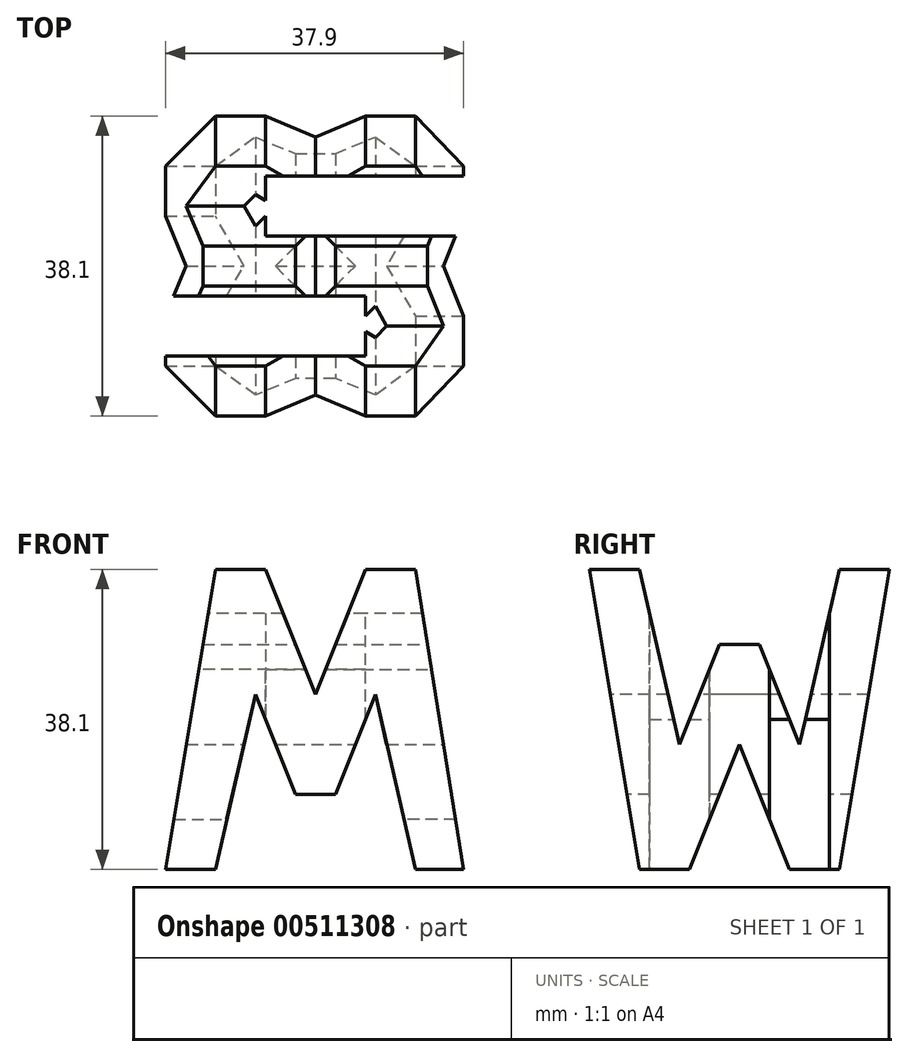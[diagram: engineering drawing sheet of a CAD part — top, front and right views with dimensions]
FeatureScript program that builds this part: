
annotation { "Feature Type Name" : "Feature", "Feature Type Description" : "" }
export const myFeature = defineFeature(function(context is Context, id is Id, definition is map)
    precondition{}
    {
        {
            var Q0;
            Q0=qCreatedBy(makeId("Front.planeOp"),FACE);
            var sketch = newSketch(context, id + "F0", { "sketchPlane" : qUnion([Q0])});
            skLineSegment(sketch, "E0", {"start": v(0, 0) * mm, "end": v(0, 38.1) * mm});
            skLineSegment(sketch, "E1", {"start": v(0, 38.1) * mm, "end": v(38.1, 38.1) * mm});
            skLineSegment(sketch, "E2", {"start": v(38.1, 38.1) * mm, "end": v(38.1, 0) * mm});
            skLineSegment(sketch, "E3", {"start": v(38.1, 0) * mm, "end": v(0, 0) * mm});
            skSolve(sketch);
        }
        {
            var Q0;
            Q0 = qSketchRegion(id + "F0", true);
            extrude(context, id + "F1", {"entities" : qUnion([Q0]), "depth" : 38.1 * mm, "offsetDistance" : 25.4 * mm});
        }
        {
            var Q0;
            Q0=qCreatedBy(makeId("Front.planeOp"),FACE);
            cPlane(context, id + "F2", {"entities" : qUnion([Q0]), "cplaneType" : CPlaneType.OFFSET, "offset" : 38.1 * mm, "width" : 152.4 * mm, "height" : 152.4 * mm});
        }
        {
            var Q0;
            Q0=qCreatedBy(makeId("Top.planeOp"),FACE);
            cPlane(context, id + "F3", {"entities" : qUnion([Q0]), "cplaneType" : CPlaneType.OFFSET, "offset" : 38.1 * mm, "width" : 152.4 * mm, "height" : 152.4 * mm});
        }
        {
            var Q0;
            Q0=makeQuery(id+"F1.opExtrude","SWEPT_FACE",FACE,{"disambiguationData":[OSD([sQuery(id+"F0.wireOp",EDGE,"E2")])]});
            var sketch = newSketch(context, id + "F4", { "sketchPlane" : qUnion([Q0])});
            skLineSegment(sketch, "E4", {"start": v(-38.1, 38.1) * mm, "end": v(-31.75, 38.1) * mm});
            skLineSegment(sketch, "E5", {"start": v(-31.75, 38.1) * mm, "end": v(-26.67, 15.88) * mm});
            skLineSegment(sketch, "E6", {"start": v(-38.1, 38.1) * mm, "end": v(-31.75, 0) * mm});
            skLineSegment(sketch, "E7", {"start": v(-31.75, 0) * mm, "end": v(-25.4, 0) * mm});
            skLineSegment(sketch, "E8", {"start": v(-25.4, 0) * mm, "end": v(-19.05, 15.88) * mm});
            skLineSegment(sketch, "E9", {"start": v(-19.05, 15.88) * mm, "end": v(-12.7, 0) * mm});
            skLineSegment(sketch, "E10", {"start": v(-12.7, 0) * mm, "end": v(-6.35, 0) * mm});
            skLineSegment(sketch, "E11", {"start": v(-6.35, 0) * mm, "end": v(0, 38.1) * mm});
            skLineSegment(sketch, "E12", {"start": v(0, 38.1) * mm, "end": v(-6.35, 38.1) * mm});
            skLineSegment(sketch, "E13", {"start": v(-6.35, 38.1) * mm, "end": v(-11.43, 15.88) * mm});
            skLineSegment(sketch, "E14", {"start": v(-11.43, 15.88) * mm, "end": v(-16.5, 28.58) * mm});
            skLineSegment(sketch, "E15", {"start": v(-16.5, 28.58) * mm, "end": v(-21.59, 28.58) * mm});
            skLineSegment(sketch, "E16", {"start": v(-21.59, 28.58) * mm, "end": v(-26.67, 15.88) * mm});
            skSolve(sketch);
        }
        {
            var Q0;
            {var subQ1=sQuery(id+"F4.wireOp",EDGE,"E5");Q0=makeQuery(id+"F4.imprint","IMPRINT",FACE,{"disambiguationData":[TD([[makeQuery(id+"F4.imprint","IMPRINT",EDGE,{"derivedFrom":subQ1}),1.0]])]});}
            var Q1;
            {var subQ0=sQuery(id+"F4.wireOp",EDGE,"E6");Q1=makeQuery(id+"F4.imprint","IMPRINT",FACE,{"disambiguationData":[TD([[makeQuery(id+"F4.imprint","IMPRINT",EDGE,{"derivedFrom":subQ0}),-1.0]])]});}
            var Q2;
            {var subQ0=sQuery(id+"F4.wireOp",EDGE,"E8");Q2=makeQuery(id+"F4.imprint","IMPRINT",FACE,{"disambiguationData":[TD([[makeQuery(id+"F4.imprint","IMPRINT",EDGE,{"derivedFrom":subQ0}),-1.0]])]});}
            var Q3;
            {var subQ0=sQuery(id+"F4.wireOp",EDGE,"E11");Q3=makeQuery(id+"F4.imprint","IMPRINT",FACE,{"disambiguationData":[TD([[makeQuery(id+"F4.imprint","IMPRINT",EDGE,{"derivedFrom":subQ0}),-1.0]])]});}
            extrude(context, id + "F5", {"entities" : qUnion([Q0, Q1, Q2, Q3]), "operationType" : NewBodyOperationType.REMOVE, "oppositeDirection" : true, "depth" : 38.1 * mm, "offsetDistance" : 25.4 * mm});
        }
        {
            var Q0;
            Q0=qCreatedBy(id+"F2.planeOp",FACE);
            var sketch = newSketch(context, id + "F6", { "sketchPlane" : qUnion([Q0])});
            skLineSegment(sketch, "E17", {"start": v(6.35, 38.1) * mm, "end": v(12.7, 38.1) * mm});
            skLineSegment(sketch, "E18", {"start": v(12.7, 38.1) * mm, "end": v(19.05, 22.22) * mm});
            skLineSegment(sketch, "E19", {"start": v(19.05, 22.22) * mm, "end": v(25.4, 38.1) * mm});
            skLineSegment(sketch, "E20", {"start": v(25.4, 38.1) * mm, "end": v(31.75, 38.1) * mm});
            skLineSegment(sketch, "E21", {"start": v(31.75, 38.1) * mm, "end": v(37.9, 0) * mm});
            skLineSegment(sketch, "E22", {"start": v(37.9, 0) * mm, "end": v(31.75, 0) * mm});
            skLineSegment(sketch, "E23", {"start": v(31.75, 0) * mm, "end": v(26.67, 22.22) * mm});
            skLineSegment(sketch, "E24", {"start": v(26.67, 22.22) * mm, "end": v(21.6, 9.52) * mm});
            skLineSegment(sketch, "E25", {"start": v(21.59, 9.52) * mm, "end": v(16.51, 9.52) * mm});
            skLineSegment(sketch, "E26", {"start": v(16.51, 9.52) * mm, "end": v(11.43, 22.22) * mm});
            skLineSegment(sketch, "E27", {"start": v(11.43, 22.22) * mm, "end": v(6.35, 0) * mm});
            skLineSegment(sketch, "E28", {"start": v(6.35, 0) * mm, "end": v(0, 0) * mm});
            skLineSegment(sketch, "E29", {"start": v(0, 0) * mm, "end": v(6.35, 38.1) * mm});
            skLineSegment(sketch, "E30.bottom", {"start": v(0, 0) * mm, "end": v(38.1, 0) * mm});
            skLineSegment(sketch, "E30.top", {"start": v(0, 38.1) * mm, "end": v(38.1, 38.1) * mm});
            skLineSegment(sketch, "E30.left", {"start": v(0, 0) * mm, "end": v(0, 38.1) * mm});
            skLineSegment(sketch, "E30.right", {"start": v(38.1, 0) * mm, "end": v(38.1, 38.1) * mm});
            skSolve(sketch);
        }
        {
            var Q0;
            {var subQ0=sQuery(id+"F6.wireOp",EDGE,"E29");Q0=makeQuery(id+"F6.imprint","IMPRINT",FACE,{"disambiguationData":[TD([[makeQuery(id+"F6.imprint","IMPRINT",EDGE,{"derivedFrom":subQ0}),1.0]])]});}
            var Q1;
            {var subQ0=sQuery(id+"F6.wireOp",EDGE,"E18");Q1=makeQuery(id+"F6.imprint","IMPRINT",FACE,{"disambiguationData":[TD([[makeQuery(id+"F6.imprint","IMPRINT",EDGE,{"derivedFrom":subQ0}),1.0]])]});}
            var Q2;
            {var subQ0=sQuery(id+"F6.wireOp",EDGE,"E23");Q2=makeQuery(id+"F6.imprint","IMPRINT",FACE,{"disambiguationData":[TD([[makeQuery(id+"F6.imprint","IMPRINT",EDGE,{"derivedFrom":subQ0}),1.0]])]});}
            var Q3;
            {var subQ0=sQuery(id+"F6.wireOp",EDGE,"E21");Q3=makeQuery(id+"F6.imprint","IMPRINT",FACE,{"disambiguationData":[TD([[makeQuery(id+"F6.imprint","IMPRINT",EDGE,{"derivedFrom":subQ0}),1.0]])]});}
            extrude(context, id + "F7", {"entities" : qUnion([Q0, Q1, Q2, Q3]), "operationType" : NewBodyOperationType.REMOVE, "oppositeDirection" : true, "depth" : 38.1 * mm, "offsetDistance" : 25.4 * mm});
        }
        {
            var Q0;
            Q0=qCreatedBy(id+"F3.planeOp",FACE);
            var sketch = newSketch(context, id + "F8", { "sketchPlane" : qUnion([Q0])});
            skLineSegment(sketch, "E31.bottom", {"start": v(0, -38.1) * mm, "end": v(38.1, -38.1) * mm});
            skLineSegment(sketch, "E31.top", {"start": v(0, 0) * mm, "end": v(38.1, 0) * mm});
            skLineSegment(sketch, "E31.left", {"start": v(0, -38.1) * mm, "end": v(0, 0) * mm});
            skLineSegment(sketch, "E31.right", {"start": v(38.1, -38.1) * mm, "end": v(38.1, 0) * mm});
            skLineSegment(sketch, "E32", {"start": v(12.7, -7.62) * mm, "end": v(12.7, -15.24) * mm});
            skLineSegment(sketch, "E33", {"start": v(12.7, -15.24) * mm, "end": v(38.1, -15.24) * mm});
            skLineSegment(sketch, "E34", {"start": v(38.1, -15.24) * mm, "end": v(38.1, -7.62) * mm});
            skLineSegment(sketch, "E35", {"start": v(38.1, -7.62) * mm, "end": v(12.7, -7.62) * mm});
            skLineSegment(sketch, "E36", {"start": v(25.4, -22.86) * mm, "end": v(0, -22.86) * mm});
            skLineSegment(sketch, "E37", {"start": v(0, -22.86) * mm, "end": v(0, -30.48) * mm});
            skLineSegment(sketch, "E38", {"start": v(0, -30.48) * mm, "end": v(25.4, -30.48) * mm});
            skLineSegment(sketch, "E39", {"start": v(25.4, -30.48) * mm, "end": v(25.4, -22.86) * mm});
            skSolve(sketch);
        }
        {
            var Q0;
            Q0=makeQuery(id+"F8.imprint","IMPRINT",FACE,{"disambiguationData":[TD([[makeQuery(id+"F8.imprint","IMPRINT",EDGE,{"derivedFrom":sQuery(id+"F8.wireOp",EDGE,"E32")}),1.0]])]});
            var Q1;
            Q1=makeQuery(id+"F8.imprint","IMPRINT",FACE,{"disambiguationData":[TD([[makeQuery(id+"F8.imprint","IMPRINT",EDGE,{"derivedFrom":sQuery(id+"F8.wireOp",EDGE,"E36")}),1.0]])]});
            extrude(context, id + "F9", {"entities" : qUnion([Q0, Q1]), "operationType" : NewBodyOperationType.REMOVE, "oppositeDirection" : true, "depth" : 38.1 * mm, "offsetDistance" : 25.4 * mm});
        }
    });
